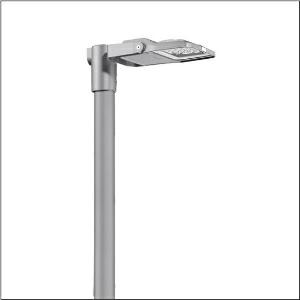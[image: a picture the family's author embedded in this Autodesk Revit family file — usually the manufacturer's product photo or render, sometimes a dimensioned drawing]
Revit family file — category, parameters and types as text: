
# Revit family: floodlight_fl_21_iq_micro___pl33t_5xa7761a2f3a_d57c
name_source: partatom
category: Lighting Fixtures
units: mm (PartAtom-declared; Revit-internal decimal feet)

## family parameters
Cut with Voids When Loaded = No
Host = Face
Light Source = No
Part Type = Normal
Room Calculation Point = No
Round Connector Dimension = Use Diameter
Shared = No

## types (1)
- --- (1 x LED, 2930 lm, 23.1 W, 3000K)
    Apparent Load = 23 VA
    CIE Flux Codes = 26 75 99 100 100
    Color Rendering = 70
    Color Temperature = 3000K
    Default Elevation = 1800 mm
    Description = Floodlight FL 21 iQ micro, floodlight, primary light control with lens, of PMMA, primary optical cover: protective disc, of toughened safety glass, transparent, light distribution: PL33T, light emission: direct distribution, installation type: surface-mounted, LED, High Power LED, rated luminous flux: 2.930lm, luminous efficacy: 127lm/W, light colour: 730, colour temperature: 3000K, control: optimised constant luminous flux control (CLO 2.0), Desk-Remote (wireless, voltage-free reading and setting of iQ features in the workshop via application-optimized NFC function/RFID function), Light-Fading, Smart-Wire, Night-Set, Lumen-Switch, Temp-Guard, Auto-Match, with terminal, 6-pole, mains connection: 220..240V, AC, 50/60Hz, start of lifetime: 23W, end of service life: 24W, reduction: 11W, luminaire housing, of diecast aluminium, powder-coated, Siteco® metallic grey (DB 702S), corrosivity category C5 mid according to DIN EN ISO 12944, sealing non-destructively replaceable, please order mast flange separately, mast bracket, of steel, galvanised, powder-coated, Siteco® metallic grey (DB 702S), protection rating (complete): IP66, insulation class (complete): insulation class II (safety insulation), certification: CE, ENEC, VDE, protection symbol: D, impact resistance: IK07, permissible operating ambient temperature: -40..+40°C, permissible operating ambient temperature for outdoor applications: -40..+50°C, standard: DIN EN 12944, LABS conformity tested according to VDMA 24364:2018-05, packaging unit: 1 piece

Light Distribution: PL33T
    Height = 65 mm
    Lamp = 1 x LED
    Lamp Light Flux = 2930 lm
    Lamp Power = 23.1 W
    Lamp count = 1
    Length = 312 mm
    Luminous efficacy = 127 lm/W
    Manufacturer = Siteco
    ModVariant = No
    Model = 5XA7761A2F3A
    Number of Poles = 1
    OnlyDefault = Yes
    Power Factor = 1
    Product Name = Floodlight FL 21 iQ micro | PL33T
    Product group = floodlight | pylon top
    ProductGroupID = 6101
    Protection Class = Protection class II
    Protection Degree = IP 66
    RLX_Detail_Level = 1
    RLX_Emergency_Light_Flux = 0 lm
    RLX_Emergency_Type = 0
    RLX_Emergency_Type_DB = No
    RlxData = <blob elided: 101625 chars, md5=43eb900f>
    Socket = socket
    Standby Power = 0 W
    System Light Flux = 2930 lm
    System Power = 23 W
    Type Comments = factory setting: luminous flux: 100 % | dim-lin: 254 | 455 mA
    Type Image = l_1007121.jpg
    URL = http://relux.com
    VarID = @adj_080709
    Voltage = 0 V
    Weight = 0.00 kg
    Width = 230 mm

## geometry (parser evidence)
native form markers: Blend x4, Sweep x11
no freeform markers — native parametric forms only
